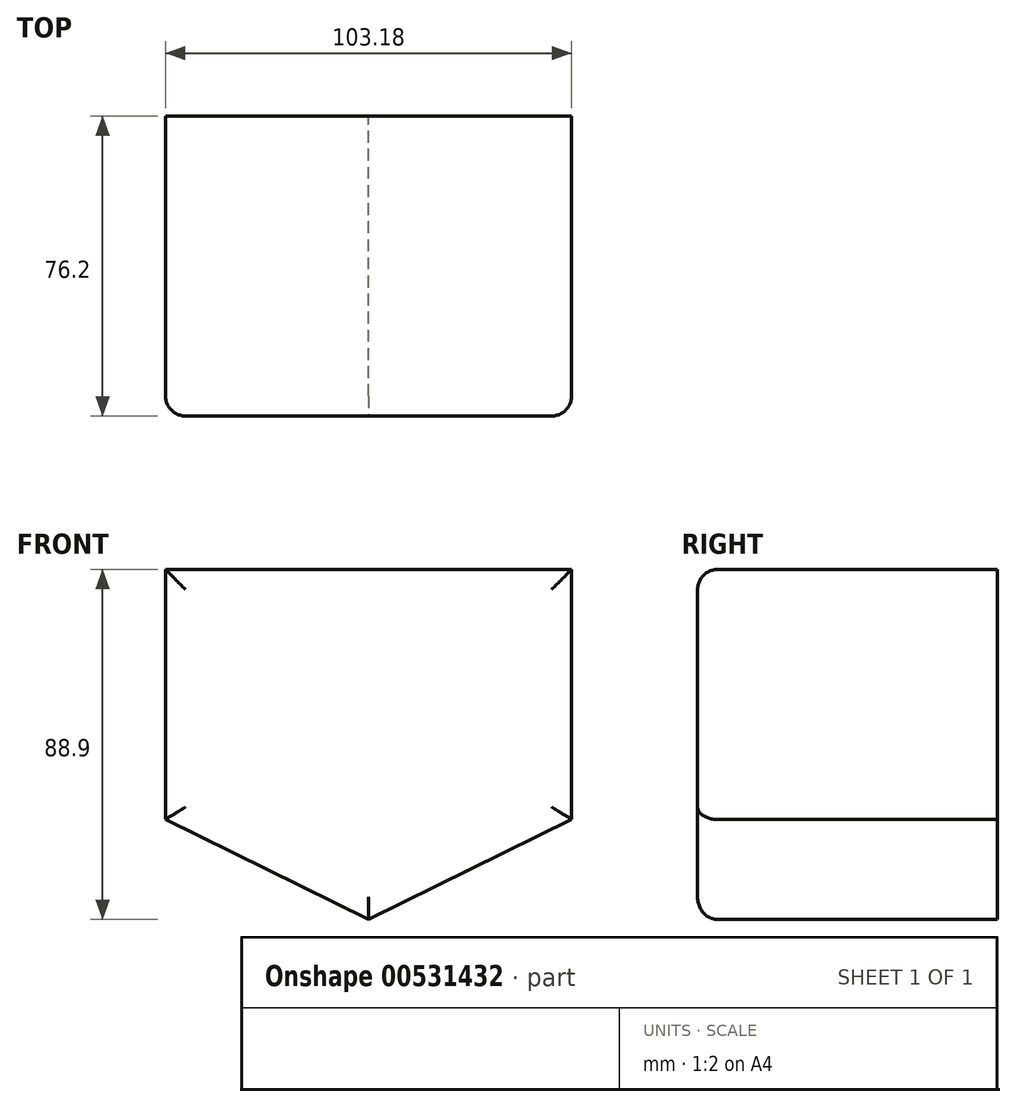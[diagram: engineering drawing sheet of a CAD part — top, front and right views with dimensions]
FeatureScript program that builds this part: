
annotation { "Feature Type Name" : "Feature", "Feature Type Description" : "" }
export const myFeature = defineFeature(function(context is Context, id is Id, definition is map)
    precondition{}
    {
        {
            var Q0;
            Q0=qCreatedBy(makeId("Front.planeOp"),FACE);
            var sketch = newSketch(context, id + "F0", { "sketchPlane" : qUnion([Q0])});
            skLineSegment(sketch, "E0.bottom", {"start": v(-51.6, 31.75) * mm, "end": v(51.6, 31.75) * mm});
            skLineSegment(sketch, "E0.top", {"start": v(-51.6, -31.75) * mm, "end": v(51.6, -31.75) * mm});
            skLineSegment(sketch, "E0.left", {"start": v(-51.6, 31.75) * mm, "end": v(-51.6, -31.75) * mm});
            skLineSegment(sketch, "E0.right", {"start": v(51.6, 31.75) * mm, "end": v(51.6, -31.75) * mm});
            skPoint(sketch, "E0.middle", {"position": v(0, 0) * mm});
            skLineSegment(sketch, "E1", {"start": v(-51.6, -31.75) * mm, "end": v(0, -57.15) * mm});
            skLineSegment(sketch, "E2", {"start": v(0, -57.15) * mm, "end": v(51.6, -31.75) * mm});
            skSolve(sketch);
        }
        {
            var Q0;
            Q0 = qSketchRegion(id + "F0", true);
            extrude(context, id + "F1", {"entities" : qUnion([Q0]), "depth" : 76.2 * mm, "offsetDistance" : 25.4 * mm});
        }
        {
            var Q0;
            Q0=makeQuery(id+"F1.opExtrude","CAP_EDGE",EDGE,{"disambiguationData":[OSD([sQuery(id+"F0.wireOp",EDGE,"E0.bottom")])],"isStart":false});
            var Q1;
            Q1=makeQuery(id+"F1.opExtrude","CAP_EDGE",EDGE,{"disambiguationData":[OSD([sQuery(id+"F0.wireOp",EDGE,"E0.left")])],"isStart":false});
            var Q2;
            Q2=makeQuery(id+"F1.opExtrude","CAP_EDGE",EDGE,{"disambiguationData":[OSD([sQuery(id+"F0.wireOp",EDGE,"E1")])],"isStart":false});
            var Q3;
            Q3=makeQuery(id+"F1.opExtrude","CAP_EDGE",EDGE,{"disambiguationData":[OSD([sQuery(id+"F0.wireOp",EDGE,"E2")])],"isStart":false});
            var Q4;
            Q4=makeQuery(id+"F1.opExtrude","CAP_EDGE",EDGE,{"disambiguationData":[OSD([sQuery(id+"F0.wireOp",EDGE,"E0.right")])],"isStart":false});
            fillet(context, id + "F2", {"entities" : qUnion([Q0, Q1, Q2, Q3, Q4]), "radius" : 5.08 * mm, "tangentPropagation" : true, "allowEdgeOverflow" : false});
        }
    });
